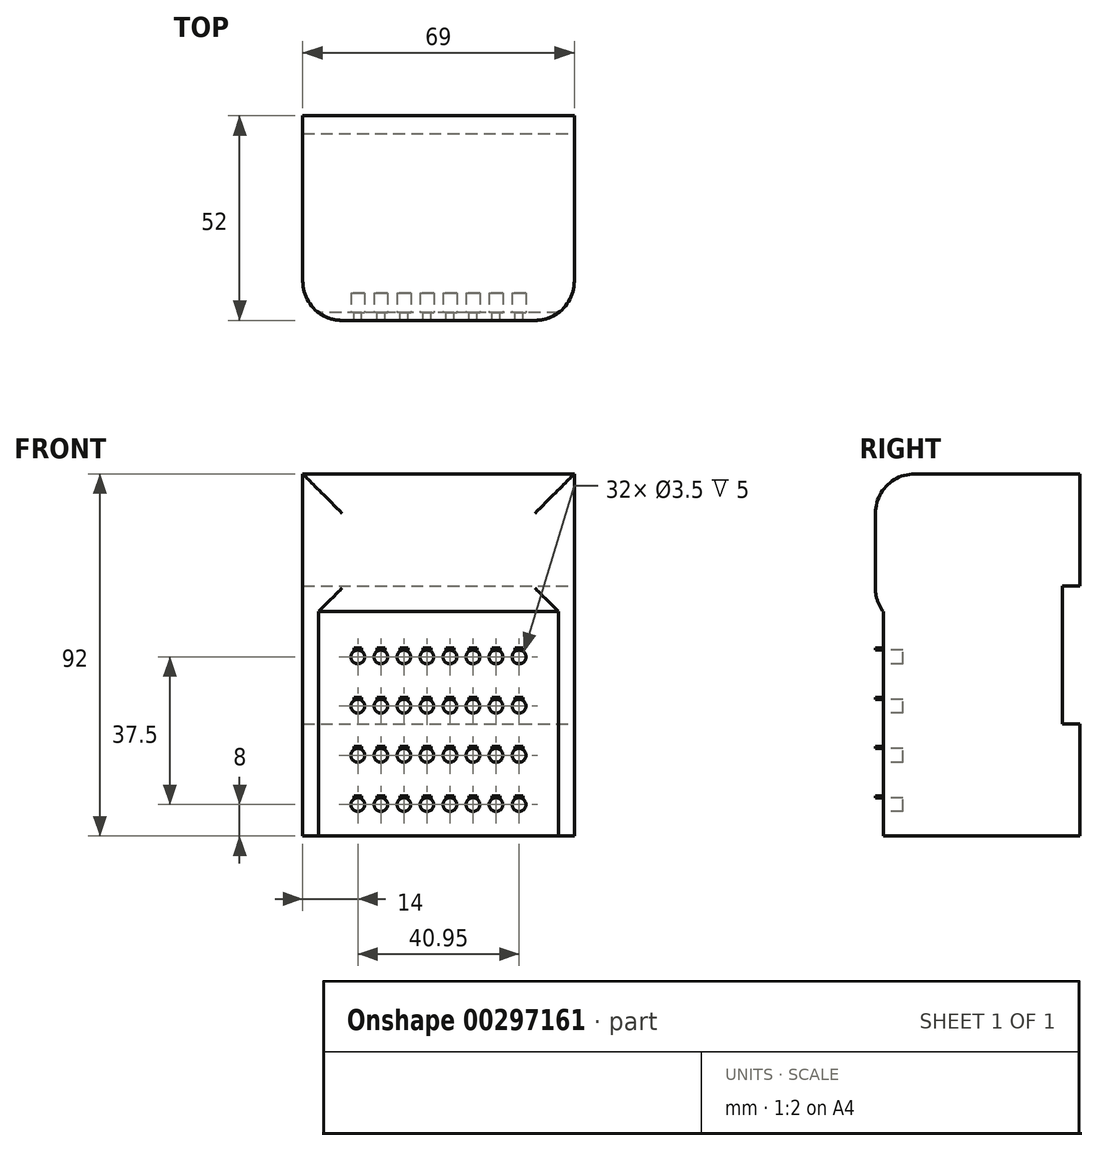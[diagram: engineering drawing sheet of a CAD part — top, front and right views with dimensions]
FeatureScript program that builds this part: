
annotation { "Feature Type Name" : "Feature", "Feature Type Description" : "" }
export const myFeature = defineFeature(function(context is Context, id is Id, definition is map)
    precondition{}
    {
        {
            var Q0;
            Q0=qCreatedBy(makeId("Front.planeOp"),FACE);
            var sketch = newSketch(context, id + "F0", { "sketchPlane" : qUnion([Q0])});
            skLineSegment(sketch, "E0.bottom", {"start": v(34.5, -46) * mm, "end": v(-34.5, -46) * mm});
            skLineSegment(sketch, "E0.top", {"start": v(34.5, 46) * mm, "end": v(-34.5, 46) * mm});
            skLineSegment(sketch, "E0.left", {"start": v(34.5, -46) * mm, "end": v(34.5, 46) * mm});
            skLineSegment(sketch, "E0.right", {"start": v(-34.5, -46) * mm, "end": v(-34.5, 46) * mm});
            skPoint(sketch, "E0.middle", {"position": v(0, 0) * mm});
            skSolve(sketch);
        }
        {
            var Q0;
            Q0=makeQuery(id+"F0.imprint","IMPRINT",FACE,{"disambiguationData":[TD([[makeQuery(id+"F0.imprint","IMPRINT",EDGE,{"derivedFrom":sQuery(id+"F0.wireOp",EDGE,"E0.bottom")}),-1.0]])]});
            extrude(context, id + "F1", {"entities" : qUnion([Q0]), "depth" : 50 * mm});
        }
        {
            var Q0;
            Q0=makeQuery(id+"F1.opExtrude","CAP_FACE",FACE,{"disambiguationData":[OSD([sQuery(id+"F0.wireOp",EDGE,"E0.bottom"),sQuery(id+"F0.wireOp",EDGE,"E0.top"),sQuery(id+"F0.wireOp",EDGE,"E0.left"),sQuery(id+"F0.wireOp",EDGE,"E0.right")])],"isStart":false});
            var sketch = newSketch(context, id + "F2", { "sketchPlane" : qUnion([Q0])});
            skLineSegment(sketch, "E1.bottom", {"start": v(-34.5, 46) * mm, "end": v(34.5, 46) * mm});
            skLineSegment(sketch, "E1.top", {"start": v(-34.5, 11) * mm, "end": v(34.5, 11) * mm});
            skLineSegment(sketch, "E1.left", {"start": v(-34.5, 46) * mm, "end": v(-34.5, 11) * mm});
            skLineSegment(sketch, "E1.right", {"start": v(34.5, 46) * mm, "end": v(34.5, 11) * mm});
            skSolve(sketch);
        }
        {
            var Q0;
            Q0=makeQuery(id+"F2.imprint","IMPRINT",FACE,{"disambiguationData":[TD([[makeQuery(id+"F2.imprint","IMPRINT",EDGE,{"derivedFrom":sQuery(id+"F2.wireOp",EDGE,"E1.bottom")}),1.0]])]});
            extrude(context, id + "F3", {"entities" : qUnion([Q0]), "operationType" : NewBodyOperationType.ADD, "depth" : 2 * mm});
        }
        {
            var Q0;
            Q0=makeQuery(id+"F3.opExtrude","CAP_FACE",FACE,{"disambiguationData":[OSD([sQuery(id+"F2.wireOp",EDGE,"E1.bottom"),sQuery(id+"F2.wireOp",EDGE,"E1.top"),sQuery(id+"F2.wireOp",EDGE,"E1.left"),sQuery(id+"F2.wireOp",EDGE,"E1.right")])],"isStart":false});
            fillet(context, id + "F4", {"entities" : qUnion([Q0]), "radius" : 10 * mm, "allowEdgeOverflow" : false});
        }
        {
            var Q0;
            Q0=makeQuery(id+"F1.opExtrude","CAP_FACE",FACE,{"disambiguationData":[OSD([sQuery(id+"F0.wireOp",EDGE,"E0.bottom"),sQuery(id+"F0.wireOp",EDGE,"E0.top"),sQuery(id+"F0.wireOp",EDGE,"E0.left"),sQuery(id+"F0.wireOp",EDGE,"E0.right")])],"isStart":false});
            var sketch = newSketch(context, id + "F5", { "sketchPlane" : qUnion([Q0])});
            skLineSegment(sketch, "E2", {"start": v(0, 11) * mm, "end": v(0, -46) * mm, "construction": true});
            skLineSegment(sketch, "E3", {"start": v(-30.5, -17.5) * mm, "end": v(30.5, -17.5) * mm, "construction": true});
            skLineSegment(sketch, "E4", {"start": v(-30.5, 11) * mm, "end": v(30.5, 11) * mm, "construction": true});
            skLineSegment(sketch, "E5", {"start": v(-30.5, -46) * mm, "end": v(30.5, -46) * mm, "construction": true});
            skLineSegment(sketch, "E6.0", {"start": v(-30.5, -0.5) * mm, "end": v(30.5, -0.5) * mm, "construction": true});
            skLineSegment(sketch, "E7.0", {"start": v(-30.5, -35) * mm, "end": v(30.5, -35) * mm, "construction": true});
            skLineSegment(sketch, "E8", {"start": v(-20.5, 11) * mm, "end": v(-20.5, -46) * mm, "construction": true});
            skLineSegment(sketch, "E9.MirrorCS", {"start": v(20.5, 11) * mm, "end": v(20.5, -46) * mm, "construction": true});
            skCircle(sketch, "E10", {"center": v(-20.5, -0.5) * mm, "radius": 1.75 * mm});
            skCircle(sketch, "E11.1.0.0", {"center": v(-14.65, -0.5) * mm, "radius": 1.75 * mm});
            skCircle(sketch, "E11.2.0.0", {"center": v(-8.8, -0.5) * mm, "radius": 1.75 * mm});
            skCircle(sketch, "E11.3.0.0", {"center": v(-2.95, -0.5) * mm, "radius": 1.75 * mm});
            skCircle(sketch, "E11.4.0.0", {"center": v(2.9, -0.5) * mm, "radius": 1.75 * mm});
            skCircle(sketch, "E11.5.0.0", {"center": v(8.75, -0.5) * mm, "radius": 1.75 * mm});
            skCircle(sketch, "E11.6.0.0", {"center": v(14.6, -0.5) * mm, "radius": 1.75 * mm});
            skCircle(sketch, "E11.7.0.0", {"center": v(20.45, -0.5) * mm, "radius": 1.75 * mm});
            skLineSegment(sketch, "E11.direction1", {"start": v(-20.5, -0.5) * mm, "end": v(-14.65, -0.5) * mm, "construction": true});
            skCircle(sketch, "E12.0.1.0", {"center": v(-20.5, -13) * mm, "radius": 1.75 * mm});
            skCircle(sketch, "E12.0.1.1", {"center": v(-14.65, -13) * mm, "radius": 1.75 * mm});
            skCircle(sketch, "E12.0.1.2", {"center": v(-8.8, -13) * mm, "radius": 1.75 * mm});
            skCircle(sketch, "E12.0.1.3", {"center": v(-2.95, -13) * mm, "radius": 1.75 * mm});
            skCircle(sketch, "E12.0.1.4", {"center": v(2.9, -13) * mm, "radius": 1.75 * mm});
            skCircle(sketch, "E12.0.1.5", {"center": v(8.75, -13) * mm, "radius": 1.75 * mm});
            skCircle(sketch, "E12.0.1.6", {"center": v(14.6, -13) * mm, "radius": 1.75 * mm});
            skCircle(sketch, "E12.0.1.7", {"center": v(20.45, -13) * mm, "radius": 1.75 * mm});
            skCircle(sketch, "E12.0.2.0", {"center": v(-20.5, -25.5) * mm, "radius": 1.75 * mm});
            skCircle(sketch, "E12.0.2.1", {"center": v(-14.65, -25.5) * mm, "radius": 1.75 * mm});
            skCircle(sketch, "E12.0.2.2", {"center": v(-8.8, -25.5) * mm, "radius": 1.75 * mm});
            skCircle(sketch, "E12.0.2.3", {"center": v(-2.95, -25.5) * mm, "radius": 1.75 * mm});
            skCircle(sketch, "E12.0.2.4", {"center": v(2.9, -25.5) * mm, "radius": 1.75 * mm});
            skCircle(sketch, "E12.0.2.5", {"center": v(8.75, -25.5) * mm, "radius": 1.75 * mm});
            skCircle(sketch, "E12.0.2.6", {"center": v(14.6, -25.5) * mm, "radius": 1.75 * mm});
            skCircle(sketch, "E12.0.2.7", {"center": v(20.45, -25.5) * mm, "radius": 1.75 * mm});
            skCircle(sketch, "E12.0.3.0", {"center": v(-20.5, -38) * mm, "radius": 1.75 * mm});
            skCircle(sketch, "E12.0.3.1", {"center": v(-14.65, -38) * mm, "radius": 1.75 * mm});
            skCircle(sketch, "E12.0.3.2", {"center": v(-8.8, -38) * mm, "radius": 1.75 * mm});
            skCircle(sketch, "E12.0.3.3", {"center": v(-2.95, -38) * mm, "radius": 1.75 * mm});
            skCircle(sketch, "E12.0.3.4", {"center": v(2.9, -38) * mm, "radius": 1.75 * mm});
            skCircle(sketch, "E12.0.3.5", {"center": v(8.75, -38) * mm, "radius": 1.75 * mm});
            skCircle(sketch, "E12.0.3.6", {"center": v(14.6, -38) * mm, "radius": 1.75 * mm});
            skCircle(sketch, "E12.0.3.7", {"center": v(20.45, -38) * mm, "radius": 1.75 * mm});
            skLineSegment(sketch, "E12.direction1", {"start": v(-20.5, -0.5) * mm, "end": v(47.4, -0.5) * mm, "construction": true});
            skLineSegment(sketch, "E12.direction2", {"start": v(-20.5, -0.5) * mm, "end": v(-20.5, -13) * mm, "construction": true});
            skLineSegment(sketch, "E13", {"start": v(-20.5, 1.25) * mm, "end": v(-19.5, 1.25) * mm});
            skLineSegment(sketch, "E14", {"start": v(-19.5, 1.25) * mm, "end": v(-19.5, 1.75) * mm});
            skLineSegment(sketch, "E15", {"start": v(-19.5, 1.75) * mm, "end": v(-21.5, 1.75) * mm});
            skLineSegment(sketch, "E16", {"start": v(-21.5, 1.75) * mm, "end": v(-21.5, 1.25) * mm});
            skLineSegment(sketch, "E17", {"start": v(-21.5, 1.25) * mm, "end": v(-20.5, 1.25) * mm});
            skLineSegment(sketch, "E18.0.1.0", {"start": v(-21.5, -10.75) * mm, "end": v(-21.5, -11.25) * mm});
            skLineSegment(sketch, "E18.0.1.1", {"start": v(-19.5, -10.75) * mm, "end": v(-21.5, -10.75) * mm});
            skLineSegment(sketch, "E18.0.1.2", {"start": v(-19.5, -11.25) * mm, "end": v(-19.5, -10.75) * mm});
            skLineSegment(sketch, "E18.0.1.3", {"start": v(-20.5, -11.25) * mm, "end": v(-19.5, -11.25) * mm});
            skLineSegment(sketch, "E18.0.1.4", {"start": v(-21.5, -11.25) * mm, "end": v(-20.5, -11.25) * mm});
            skLineSegment(sketch, "E18.0.2.0", {"start": v(-21.5, -23.25) * mm, "end": v(-21.5, -23.75) * mm});
            skLineSegment(sketch, "E18.0.2.1", {"start": v(-19.5, -23.25) * mm, "end": v(-21.5, -23.25) * mm});
            skLineSegment(sketch, "E18.0.2.2", {"start": v(-19.5, -23.75) * mm, "end": v(-19.5, -23.25) * mm});
            skLineSegment(sketch, "E18.0.2.3", {"start": v(-20.5, -23.75) * mm, "end": v(-19.5, -23.75) * mm});
            skLineSegment(sketch, "E18.0.2.4", {"start": v(-21.5, -23.75) * mm, "end": v(-20.5, -23.75) * mm});
            skLineSegment(sketch, "E18.0.3.0", {"start": v(-21.5, -35.75) * mm, "end": v(-21.5, -36.25) * mm});
            skLineSegment(sketch, "E18.0.3.1", {"start": v(-19.5, -35.75) * mm, "end": v(-21.5, -35.75) * mm});
            skLineSegment(sketch, "E18.0.3.2", {"start": v(-19.5, -36.25) * mm, "end": v(-19.5, -35.75) * mm});
            skLineSegment(sketch, "E18.0.3.3", {"start": v(-20.5, -36.25) * mm, "end": v(-19.5, -36.25) * mm});
            skLineSegment(sketch, "E18.0.3.4", {"start": v(-21.5, -36.25) * mm, "end": v(-20.5, -36.25) * mm});
            skLineSegment(sketch, "E18.1.0.0", {"start": v(-15.65, 1.75) * mm, "end": v(-15.65, 1.25) * mm});
            skLineSegment(sketch, "E18.1.0.1", {"start": v(-13.65, 1.75) * mm, "end": v(-15.65, 1.75) * mm});
            skLineSegment(sketch, "E18.1.0.2", {"start": v(-13.65, 1.25) * mm, "end": v(-13.65, 1.75) * mm});
            skLineSegment(sketch, "E18.1.0.3", {"start": v(-14.65, 1.25) * mm, "end": v(-13.65, 1.25) * mm});
            skLineSegment(sketch, "E18.1.0.4", {"start": v(-15.65, 1.25) * mm, "end": v(-14.65, 1.25) * mm});
            skLineSegment(sketch, "E18.1.1.0", {"start": v(-15.65, -10.75) * mm, "end": v(-15.65, -11.25) * mm});
            skLineSegment(sketch, "E18.1.1.1", {"start": v(-13.65, -10.75) * mm, "end": v(-15.65, -10.75) * mm});
            skLineSegment(sketch, "E18.1.1.2", {"start": v(-13.65, -11.25) * mm, "end": v(-13.65, -10.75) * mm});
            skLineSegment(sketch, "E18.1.1.3", {"start": v(-14.65, -11.25) * mm, "end": v(-13.65, -11.25) * mm});
            skLineSegment(sketch, "E18.1.1.4", {"start": v(-15.65, -11.25) * mm, "end": v(-14.65, -11.25) * mm});
            skLineSegment(sketch, "E18.1.2.0", {"start": v(-15.65, -23.25) * mm, "end": v(-15.65, -23.75) * mm});
            skLineSegment(sketch, "E18.1.2.1", {"start": v(-13.65, -23.25) * mm, "end": v(-15.65, -23.25) * mm});
            skLineSegment(sketch, "E18.1.2.2", {"start": v(-13.65, -23.75) * mm, "end": v(-13.65, -23.25) * mm});
            skLineSegment(sketch, "E18.1.2.3", {"start": v(-14.65, -23.75) * mm, "end": v(-13.65, -23.75) * mm});
            skLineSegment(sketch, "E18.1.2.4", {"start": v(-15.65, -23.75) * mm, "end": v(-14.65, -23.75) * mm});
            skLineSegment(sketch, "E18.1.3.0", {"start": v(-15.65, -35.75) * mm, "end": v(-15.65, -36.25) * mm});
            skLineSegment(sketch, "E18.1.3.1", {"start": v(-13.65, -35.75) * mm, "end": v(-15.65, -35.75) * mm});
            skLineSegment(sketch, "E18.1.3.2", {"start": v(-13.65, -36.25) * mm, "end": v(-13.65, -35.75) * mm});
            skLineSegment(sketch, "E18.1.3.3", {"start": v(-14.65, -36.25) * mm, "end": v(-13.65, -36.25) * mm});
            skLineSegment(sketch, "E18.1.3.4", {"start": v(-15.65, -36.25) * mm, "end": v(-14.65, -36.25) * mm});
            skLineSegment(sketch, "E18.2.0.0", {"start": v(-9.8, 1.75) * mm, "end": v(-9.8, 1.25) * mm});
            skLineSegment(sketch, "E18.2.0.1", {"start": v(-7.8, 1.75) * mm, "end": v(-9.8, 1.75) * mm});
            skLineSegment(sketch, "E18.2.0.2", {"start": v(-7.8, 1.25) * mm, "end": v(-7.8, 1.75) * mm});
            skLineSegment(sketch, "E18.2.0.3", {"start": v(-8.8, 1.25) * mm, "end": v(-7.8, 1.25) * mm});
            skLineSegment(sketch, "E18.2.0.4", {"start": v(-9.8, 1.25) * mm, "end": v(-8.8, 1.25) * mm});
            skLineSegment(sketch, "E18.2.1.0", {"start": v(-9.8, -10.75) * mm, "end": v(-9.8, -11.25) * mm});
            skLineSegment(sketch, "E18.2.1.1", {"start": v(-7.8, -10.75) * mm, "end": v(-9.8, -10.75) * mm});
            skLineSegment(sketch, "E18.2.1.2", {"start": v(-7.8, -11.25) * mm, "end": v(-7.8, -10.75) * mm});
            skLineSegment(sketch, "E18.2.1.3", {"start": v(-8.8, -11.25) * mm, "end": v(-7.8, -11.25) * mm});
            skLineSegment(sketch, "E18.2.1.4", {"start": v(-9.8, -11.25) * mm, "end": v(-8.8, -11.25) * mm});
            skLineSegment(sketch, "E18.2.2.0", {"start": v(-9.8, -23.25) * mm, "end": v(-9.8, -23.75) * mm});
            skLineSegment(sketch, "E18.2.2.1", {"start": v(-7.8, -23.25) * mm, "end": v(-9.8, -23.25) * mm});
            skLineSegment(sketch, "E18.2.2.2", {"start": v(-7.8, -23.75) * mm, "end": v(-7.8, -23.25) * mm});
            skLineSegment(sketch, "E18.2.2.3", {"start": v(-8.8, -23.75) * mm, "end": v(-7.8, -23.75) * mm});
            skLineSegment(sketch, "E18.2.2.4", {"start": v(-9.8, -23.75) * mm, "end": v(-8.8, -23.75) * mm});
            skLineSegment(sketch, "E18.2.3.0", {"start": v(-9.8, -35.75) * mm, "end": v(-9.8, -36.25) * mm});
            skLineSegment(sketch, "E18.2.3.1", {"start": v(-7.8, -35.75) * mm, "end": v(-9.8, -35.75) * mm});
            skLineSegment(sketch, "E18.2.3.2", {"start": v(-7.8, -36.25) * mm, "end": v(-7.8, -35.75) * mm});
            skLineSegment(sketch, "E18.2.3.3", {"start": v(-8.8, -36.25) * mm, "end": v(-7.8, -36.25) * mm});
            skLineSegment(sketch, "E18.2.3.4", {"start": v(-9.8, -36.25) * mm, "end": v(-8.8, -36.25) * mm});
            skLineSegment(sketch, "E18.3.0.0", {"start": v(-3.95, 1.75) * mm, "end": v(-3.95, 1.25) * mm});
            skLineSegment(sketch, "E18.3.0.1", {"start": v(-1.95, 1.75) * mm, "end": v(-3.95, 1.75) * mm});
            skLineSegment(sketch, "E18.3.0.2", {"start": v(-1.95, 1.25) * mm, "end": v(-1.95, 1.75) * mm});
            skLineSegment(sketch, "E18.3.0.3", {"start": v(-2.95, 1.25) * mm, "end": v(-1.95, 1.25) * mm});
            skLineSegment(sketch, "E18.3.0.4", {"start": v(-3.95, 1.25) * mm, "end": v(-2.95, 1.25) * mm});
            skLineSegment(sketch, "E18.3.1.0", {"start": v(-3.95, -10.75) * mm, "end": v(-3.95, -11.25) * mm});
            skLineSegment(sketch, "E18.3.1.1", {"start": v(-1.95, -10.75) * mm, "end": v(-3.95, -10.75) * mm});
            skLineSegment(sketch, "E18.3.1.2", {"start": v(-1.95, -11.25) * mm, "end": v(-1.95, -10.75) * mm});
            skLineSegment(sketch, "E18.3.1.3", {"start": v(-2.95, -11.25) * mm, "end": v(-1.95, -11.25) * mm});
            skLineSegment(sketch, "E18.3.1.4", {"start": v(-3.95, -11.25) * mm, "end": v(-2.95, -11.25) * mm});
            skLineSegment(sketch, "E18.3.2.0", {"start": v(-3.95, -23.25) * mm, "end": v(-3.95, -23.75) * mm});
            skLineSegment(sketch, "E18.3.2.1", {"start": v(-1.95, -23.25) * mm, "end": v(-3.95, -23.25) * mm});
            skLineSegment(sketch, "E18.3.2.2", {"start": v(-1.95, -23.75) * mm, "end": v(-1.95, -23.25) * mm});
            skLineSegment(sketch, "E18.3.2.3", {"start": v(-2.95, -23.75) * mm, "end": v(-1.95, -23.75) * mm});
            skLineSegment(sketch, "E18.3.2.4", {"start": v(-3.95, -23.75) * mm, "end": v(-2.95, -23.75) * mm});
            skLineSegment(sketch, "E18.3.3.0", {"start": v(-3.95, -35.75) * mm, "end": v(-3.95, -36.25) * mm});
            skLineSegment(sketch, "E18.3.3.1", {"start": v(-1.95, -35.75) * mm, "end": v(-3.95, -35.75) * mm});
            skLineSegment(sketch, "E18.3.3.2", {"start": v(-1.95, -36.25) * mm, "end": v(-1.95, -35.75) * mm});
            skLineSegment(sketch, "E18.3.3.3", {"start": v(-2.95, -36.25) * mm, "end": v(-1.95, -36.25) * mm});
            skLineSegment(sketch, "E18.3.3.4", {"start": v(-3.95, -36.25) * mm, "end": v(-2.95, -36.25) * mm});
            skLineSegment(sketch, "E18.4.0.0", {"start": v(1.9, 1.75) * mm, "end": v(1.9, 1.25) * mm});
            skLineSegment(sketch, "E18.4.0.1", {"start": v(3.9, 1.75) * mm, "end": v(1.9, 1.75) * mm});
            skLineSegment(sketch, "E18.4.0.2", {"start": v(3.9, 1.25) * mm, "end": v(3.9, 1.75) * mm});
            skLineSegment(sketch, "E18.4.0.3", {"start": v(2.9, 1.25) * mm, "end": v(3.9, 1.25) * mm});
            skLineSegment(sketch, "E18.4.0.4", {"start": v(1.9, 1.25) * mm, "end": v(2.9, 1.25) * mm});
            skLineSegment(sketch, "E18.4.1.0", {"start": v(1.9, -10.75) * mm, "end": v(1.9, -11.25) * mm});
            skLineSegment(sketch, "E18.4.1.1", {"start": v(3.9, -10.75) * mm, "end": v(1.9, -10.75) * mm});
            skLineSegment(sketch, "E18.4.1.2", {"start": v(3.9, -11.25) * mm, "end": v(3.9, -10.75) * mm});
            skLineSegment(sketch, "E18.4.1.3", {"start": v(2.9, -11.25) * mm, "end": v(3.9, -11.25) * mm});
            skLineSegment(sketch, "E18.4.1.4", {"start": v(1.9, -11.25) * mm, "end": v(2.9, -11.25) * mm});
            skLineSegment(sketch, "E18.4.2.0", {"start": v(1.9, -23.25) * mm, "end": v(1.9, -23.75) * mm});
            skLineSegment(sketch, "E18.4.2.1", {"start": v(3.9, -23.25) * mm, "end": v(1.9, -23.25) * mm});
            skLineSegment(sketch, "E18.4.2.2", {"start": v(3.9, -23.75) * mm, "end": v(3.9, -23.25) * mm});
            skLineSegment(sketch, "E18.4.2.3", {"start": v(2.9, -23.75) * mm, "end": v(3.9, -23.75) * mm});
            skLineSegment(sketch, "E18.4.2.4", {"start": v(1.9, -23.75) * mm, "end": v(2.9, -23.75) * mm});
            skLineSegment(sketch, "E18.4.3.0", {"start": v(1.9, -35.75) * mm, "end": v(1.9, -36.25) * mm});
            skLineSegment(sketch, "E18.4.3.1", {"start": v(3.9, -35.75) * mm, "end": v(1.9, -35.75) * mm});
            skLineSegment(sketch, "E18.4.3.2", {"start": v(3.9, -36.25) * mm, "end": v(3.9, -35.75) * mm});
            skLineSegment(sketch, "E18.4.3.3", {"start": v(2.9, -36.25) * mm, "end": v(3.9, -36.25) * mm});
            skLineSegment(sketch, "E18.4.3.4", {"start": v(1.9, -36.25) * mm, "end": v(2.9, -36.25) * mm});
            skLineSegment(sketch, "E18.5.0.0", {"start": v(7.75, 1.75) * mm, "end": v(7.75, 1.25) * mm});
            skLineSegment(sketch, "E18.5.0.1", {"start": v(9.75, 1.75) * mm, "end": v(7.75, 1.75) * mm});
            skLineSegment(sketch, "E18.5.0.2", {"start": v(9.75, 1.25) * mm, "end": v(9.75, 1.75) * mm});
            skLineSegment(sketch, "E18.5.0.3", {"start": v(8.75, 1.25) * mm, "end": v(9.75, 1.25) * mm});
            skLineSegment(sketch, "E18.5.0.4", {"start": v(7.75, 1.25) * mm, "end": v(8.75, 1.25) * mm});
            skLineSegment(sketch, "E18.5.1.0", {"start": v(7.75, -10.75) * mm, "end": v(7.75, -11.25) * mm});
            skLineSegment(sketch, "E18.5.1.1", {"start": v(9.75, -10.75) * mm, "end": v(7.75, -10.75) * mm});
            skLineSegment(sketch, "E18.5.1.2", {"start": v(9.75, -11.25) * mm, "end": v(9.75, -10.75) * mm});
            skLineSegment(sketch, "E18.5.1.3", {"start": v(8.75, -11.25) * mm, "end": v(9.75, -11.25) * mm});
            skLineSegment(sketch, "E18.5.1.4", {"start": v(7.75, -11.25) * mm, "end": v(8.75, -11.25) * mm});
            skLineSegment(sketch, "E18.5.2.0", {"start": v(7.75, -23.25) * mm, "end": v(7.75, -23.75) * mm});
            skLineSegment(sketch, "E18.5.2.1", {"start": v(9.75, -23.25) * mm, "end": v(7.75, -23.25) * mm});
            skLineSegment(sketch, "E18.5.2.2", {"start": v(9.75, -23.75) * mm, "end": v(9.75, -23.25) * mm});
            skLineSegment(sketch, "E18.5.2.3", {"start": v(8.75, -23.75) * mm, "end": v(9.75, -23.75) * mm});
            skLineSegment(sketch, "E18.5.2.4", {"start": v(7.75, -23.75) * mm, "end": v(8.75, -23.75) * mm});
            skLineSegment(sketch, "E18.5.3.0", {"start": v(7.75, -35.75) * mm, "end": v(7.75, -36.25) * mm});
            skLineSegment(sketch, "E18.5.3.1", {"start": v(9.75, -35.75) * mm, "end": v(7.75, -35.75) * mm});
            skLineSegment(sketch, "E18.5.3.2", {"start": v(9.75, -36.25) * mm, "end": v(9.75, -35.75) * mm});
            skLineSegment(sketch, "E18.5.3.3", {"start": v(8.75, -36.25) * mm, "end": v(9.75, -36.25) * mm});
            skLineSegment(sketch, "E18.5.3.4", {"start": v(7.75, -36.25) * mm, "end": v(8.75, -36.25) * mm});
            skLineSegment(sketch, "E18.6.0.0", {"start": v(13.6, 1.75) * mm, "end": v(13.6, 1.25) * mm});
            skLineSegment(sketch, "E18.6.0.1", {"start": v(15.6, 1.75) * mm, "end": v(13.6, 1.75) * mm});
            skLineSegment(sketch, "E18.6.0.2", {"start": v(15.6, 1.25) * mm, "end": v(15.6, 1.75) * mm});
            skLineSegment(sketch, "E18.6.0.3", {"start": v(14.6, 1.25) * mm, "end": v(15.6, 1.25) * mm});
            skLineSegment(sketch, "E18.6.0.4", {"start": v(13.6, 1.25) * mm, "end": v(14.6, 1.25) * mm});
            skLineSegment(sketch, "E18.6.1.0", {"start": v(13.6, -10.75) * mm, "end": v(13.6, -11.25) * mm});
            skLineSegment(sketch, "E18.6.1.1", {"start": v(15.6, -10.75) * mm, "end": v(13.6, -10.75) * mm});
            skLineSegment(sketch, "E18.6.1.2", {"start": v(15.6, -11.25) * mm, "end": v(15.6, -10.75) * mm});
            skLineSegment(sketch, "E18.6.1.3", {"start": v(14.6, -11.25) * mm, "end": v(15.6, -11.25) * mm});
            skLineSegment(sketch, "E18.6.1.4", {"start": v(13.6, -11.25) * mm, "end": v(14.6, -11.25) * mm});
            skLineSegment(sketch, "E18.6.2.0", {"start": v(13.6, -23.25) * mm, "end": v(13.6, -23.75) * mm});
            skLineSegment(sketch, "E18.6.2.1", {"start": v(15.6, -23.25) * mm, "end": v(13.6, -23.25) * mm});
            skLineSegment(sketch, "E18.6.2.2", {"start": v(15.6, -23.75) * mm, "end": v(15.6, -23.25) * mm});
            skLineSegment(sketch, "E18.6.2.3", {"start": v(14.6, -23.75) * mm, "end": v(15.6, -23.75) * mm});
            skLineSegment(sketch, "E18.6.2.4", {"start": v(13.6, -23.75) * mm, "end": v(14.6, -23.75) * mm});
            skLineSegment(sketch, "E18.6.3.0", {"start": v(13.6, -35.75) * mm, "end": v(13.6, -36.25) * mm});
            skLineSegment(sketch, "E18.6.3.1", {"start": v(15.6, -35.75) * mm, "end": v(13.6, -35.75) * mm});
            skLineSegment(sketch, "E18.6.3.2", {"start": v(15.6, -36.25) * mm, "end": v(15.6, -35.75) * mm});
            skLineSegment(sketch, "E18.6.3.3", {"start": v(14.6, -36.25) * mm, "end": v(15.6, -36.25) * mm});
            skLineSegment(sketch, "E18.6.3.4", {"start": v(13.6, -36.25) * mm, "end": v(14.6, -36.25) * mm});
            skLineSegment(sketch, "E18.7.0.0", {"start": v(19.45, 1.75) * mm, "end": v(19.45, 1.25) * mm});
            skLineSegment(sketch, "E18.7.0.1", {"start": v(21.45, 1.75) * mm, "end": v(19.45, 1.75) * mm});
            skLineSegment(sketch, "E18.7.0.2", {"start": v(21.45, 1.25) * mm, "end": v(21.45, 1.75) * mm});
            skLineSegment(sketch, "E18.7.0.3", {"start": v(20.45, 1.25) * mm, "end": v(21.45, 1.25) * mm});
            skLineSegment(sketch, "E18.7.0.4", {"start": v(19.45, 1.25) * mm, "end": v(20.45, 1.25) * mm});
            skLineSegment(sketch, "E18.7.1.0", {"start": v(19.45, -10.75) * mm, "end": v(19.45, -11.25) * mm});
            skLineSegment(sketch, "E18.7.1.1", {"start": v(21.45, -10.75) * mm, "end": v(19.45, -10.75) * mm});
            skLineSegment(sketch, "E18.7.1.2", {"start": v(21.45, -11.25) * mm, "end": v(21.45, -10.75) * mm});
            skLineSegment(sketch, "E18.7.1.3", {"start": v(20.45, -11.25) * mm, "end": v(21.45, -11.25) * mm});
            skLineSegment(sketch, "E18.7.1.4", {"start": v(19.45, -11.25) * mm, "end": v(20.45, -11.25) * mm});
            skLineSegment(sketch, "E18.7.2.0", {"start": v(19.45, -23.25) * mm, "end": v(19.45, -23.75) * mm});
            skLineSegment(sketch, "E18.7.2.1", {"start": v(21.45, -23.25) * mm, "end": v(19.45, -23.25) * mm});
            skLineSegment(sketch, "E18.7.2.2", {"start": v(21.45, -23.75) * mm, "end": v(21.45, -23.25) * mm});
            skLineSegment(sketch, "E18.7.2.3", {"start": v(20.45, -23.75) * mm, "end": v(21.45, -23.75) * mm});
            skLineSegment(sketch, "E18.7.2.4", {"start": v(19.45, -23.75) * mm, "end": v(20.45, -23.75) * mm});
            skLineSegment(sketch, "E18.7.3.0", {"start": v(19.45, -35.75) * mm, "end": v(19.45, -36.25) * mm});
            skLineSegment(sketch, "E18.7.3.1", {"start": v(21.45, -35.75) * mm, "end": v(19.45, -35.75) * mm});
            skLineSegment(sketch, "E18.7.3.2", {"start": v(21.45, -36.25) * mm, "end": v(21.45, -35.75) * mm});
            skLineSegment(sketch, "E18.7.3.3", {"start": v(20.45, -36.25) * mm, "end": v(21.45, -36.25) * mm});
            skLineSegment(sketch, "E18.7.3.4", {"start": v(19.45, -36.25) * mm, "end": v(20.45, -36.25) * mm});
            skLineSegment(sketch, "E18.direction1", {"start": v(-21.5, 1.25) * mm, "end": v(-15.65, 1.25) * mm, "construction": true});
            skLineSegment(sketch, "E18.direction2", {"start": v(-21.5, 1.25) * mm, "end": v(-21.5, -11.25) * mm, "construction": true});
            skSolve(sketch);
        }
        {
            var Q0;
            Q0=makeQuery(id+"F5.imprint","IMPRINT",FACE,{"disambiguationData":[TD([[makeQuery(id+"F5.imprint","IMPRINT",EDGE,{"derivedFrom":sQuery(id+"F5.wireOp",EDGE,"E10")}),1.0]])]});
            var Q1;
            Q1=makeQuery(id+"F5.imprint","IMPRINT",FACE,{"disambiguationData":[TD([[makeQuery(id+"F5.imprint","IMPRINT",EDGE,{"derivedFrom":sQuery(id+"F5.wireOp",EDGE,"E11.1.0.0")}),1.0]])]});
            var Q2;
            Q2=makeQuery(id+"F5.imprint","IMPRINT",FACE,{"disambiguationData":[TD([[makeQuery(id+"F5.imprint","IMPRINT",EDGE,{"derivedFrom":sQuery(id+"F5.wireOp",EDGE,"E11.2.0.0")}),1.0]])]});
            var Q3;
            Q3=makeQuery(id+"F5.imprint","IMPRINT",FACE,{"disambiguationData":[TD([[makeQuery(id+"F5.imprint","IMPRINT",EDGE,{"derivedFrom":sQuery(id+"F5.wireOp",EDGE,"E11.3.0.0")}),1.0]])]});
            var Q4;
            Q4=makeQuery(id+"F5.imprint","IMPRINT",FACE,{"disambiguationData":[TD([[makeQuery(id+"F5.imprint","IMPRINT",EDGE,{"derivedFrom":sQuery(id+"F5.wireOp",EDGE,"E11.4.0.0")}),1.0]])]});
            var Q5;
            Q5=makeQuery(id+"F5.imprint","IMPRINT",FACE,{"disambiguationData":[TD([[makeQuery(id+"F5.imprint","IMPRINT",EDGE,{"derivedFrom":sQuery(id+"F5.wireOp",EDGE,"E11.5.0.0")}),1.0]])]});
            var Q6;
            Q6=makeQuery(id+"F5.imprint","IMPRINT",FACE,{"disambiguationData":[TD([[makeQuery(id+"F5.imprint","IMPRINT",EDGE,{"derivedFrom":sQuery(id+"F5.wireOp",EDGE,"E11.6.0.0")}),1.0]])]});
            var Q7;
            Q7=makeQuery(id+"F5.imprint","IMPRINT",FACE,{"disambiguationData":[TD([[makeQuery(id+"F5.imprint","IMPRINT",EDGE,{"derivedFrom":sQuery(id+"F5.wireOp",EDGE,"E11.7.0.0")}),1.0]])]});
            var Q8;
            Q8=makeQuery(id+"F5.imprint","IMPRINT",FACE,{"disambiguationData":[TD([[makeQuery(id+"F5.imprint","IMPRINT",EDGE,{"derivedFrom":sQuery(id+"F5.wireOp",EDGE,"E12.0.1.0")}),1.0]])]});
            var Q9;
            Q9=makeQuery(id+"F5.imprint","IMPRINT",FACE,{"disambiguationData":[TD([[makeQuery(id+"F5.imprint","IMPRINT",EDGE,{"derivedFrom":sQuery(id+"F5.wireOp",EDGE,"E12.0.1.1")}),1.0]])]});
            var Q10;
            Q10=makeQuery(id+"F5.imprint","IMPRINT",FACE,{"disambiguationData":[TD([[makeQuery(id+"F5.imprint","IMPRINT",EDGE,{"derivedFrom":sQuery(id+"F5.wireOp",EDGE,"E12.0.1.2")}),1.0]])]});
            var Q11;
            Q11=makeQuery(id+"F5.imprint","IMPRINT",FACE,{"disambiguationData":[TD([[makeQuery(id+"F5.imprint","IMPRINT",EDGE,{"derivedFrom":sQuery(id+"F5.wireOp",EDGE,"E12.0.1.3")}),1.0]])]});
            var Q12;
            Q12=makeQuery(id+"F5.imprint","IMPRINT",FACE,{"disambiguationData":[TD([[makeQuery(id+"F5.imprint","IMPRINT",EDGE,{"derivedFrom":sQuery(id+"F5.wireOp",EDGE,"E12.0.1.4")}),1.0]])]});
            var Q13;
            Q13=makeQuery(id+"F5.imprint","IMPRINT",FACE,{"disambiguationData":[TD([[makeQuery(id+"F5.imprint","IMPRINT",EDGE,{"derivedFrom":sQuery(id+"F5.wireOp",EDGE,"E12.0.1.5")}),1.0]])]});
            var Q14;
            Q14=makeQuery(id+"F5.imprint","IMPRINT",FACE,{"disambiguationData":[TD([[makeQuery(id+"F5.imprint","IMPRINT",EDGE,{"derivedFrom":sQuery(id+"F5.wireOp",EDGE,"E12.0.1.6")}),1.0]])]});
            var Q15;
            Q15=makeQuery(id+"F5.imprint","IMPRINT",FACE,{"disambiguationData":[TD([[makeQuery(id+"F5.imprint","IMPRINT",EDGE,{"derivedFrom":sQuery(id+"F5.wireOp",EDGE,"E12.0.1.7")}),1.0]])]});
            var Q16;
            Q16=makeQuery(id+"F5.imprint","IMPRINT",FACE,{"disambiguationData":[TD([[makeQuery(id+"F5.imprint","IMPRINT",EDGE,{"derivedFrom":sQuery(id+"F5.wireOp",EDGE,"E12.0.2.7")}),1.0]])]});
            var Q17;
            Q17=makeQuery(id+"F5.imprint","IMPRINT",FACE,{"disambiguationData":[TD([[makeQuery(id+"F5.imprint","IMPRINT",EDGE,{"derivedFrom":sQuery(id+"F5.wireOp",EDGE,"E12.0.2.6")}),1.0]])]});
            var Q18;
            Q18=makeQuery(id+"F5.imprint","IMPRINT",FACE,{"disambiguationData":[TD([[makeQuery(id+"F5.imprint","IMPRINT",EDGE,{"derivedFrom":sQuery(id+"F5.wireOp",EDGE,"E12.0.2.5")}),1.0]])]});
            var Q19;
            Q19=makeQuery(id+"F5.imprint","IMPRINT",FACE,{"disambiguationData":[TD([[makeQuery(id+"F5.imprint","IMPRINT",EDGE,{"derivedFrom":sQuery(id+"F5.wireOp",EDGE,"E12.0.2.4")}),1.0]])]});
            var Q20;
            Q20=makeQuery(id+"F5.imprint","IMPRINT",FACE,{"disambiguationData":[TD([[makeQuery(id+"F5.imprint","IMPRINT",EDGE,{"derivedFrom":sQuery(id+"F5.wireOp",EDGE,"E12.0.2.3")}),1.0]])]});
            var Q21;
            Q21=makeQuery(id+"F5.imprint","IMPRINT",FACE,{"disambiguationData":[TD([[makeQuery(id+"F5.imprint","IMPRINT",EDGE,{"derivedFrom":sQuery(id+"F5.wireOp",EDGE,"E12.0.2.2")}),1.0]])]});
            var Q22;
            Q22=makeQuery(id+"F5.imprint","IMPRINT",FACE,{"disambiguationData":[TD([[makeQuery(id+"F5.imprint","IMPRINT",EDGE,{"derivedFrom":sQuery(id+"F5.wireOp",EDGE,"E12.0.2.1")}),1.0]])]});
            var Q23;
            Q23=makeQuery(id+"F5.imprint","IMPRINT",FACE,{"disambiguationData":[TD([[makeQuery(id+"F5.imprint","IMPRINT",EDGE,{"derivedFrom":sQuery(id+"F5.wireOp",EDGE,"E12.0.2.0")}),1.0]])]});
            var Q24;
            Q24=makeQuery(id+"F5.imprint","IMPRINT",FACE,{"disambiguationData":[TD([[makeQuery(id+"F5.imprint","IMPRINT",EDGE,{"derivedFrom":sQuery(id+"F5.wireOp",EDGE,"E12.0.3.0")}),1.0]])]});
            var Q25;
            Q25=makeQuery(id+"F5.imprint","IMPRINT",FACE,{"disambiguationData":[TD([[makeQuery(id+"F5.imprint","IMPRINT",EDGE,{"derivedFrom":sQuery(id+"F5.wireOp",EDGE,"E12.0.3.1")}),1.0]])]});
            var Q26;
            Q26=makeQuery(id+"F5.imprint","IMPRINT",FACE,{"disambiguationData":[TD([[makeQuery(id+"F5.imprint","IMPRINT",EDGE,{"derivedFrom":sQuery(id+"F5.wireOp",EDGE,"E12.0.3.2")}),1.0]])]});
            var Q27;
            Q27=makeQuery(id+"F5.imprint","IMPRINT",FACE,{"disambiguationData":[TD([[makeQuery(id+"F5.imprint","IMPRINT",EDGE,{"derivedFrom":sQuery(id+"F5.wireOp",EDGE,"E12.0.3.3")}),1.0]])]});
            var Q28;
            Q28=makeQuery(id+"F5.imprint","IMPRINT",FACE,{"disambiguationData":[TD([[makeQuery(id+"F5.imprint","IMPRINT",EDGE,{"derivedFrom":sQuery(id+"F5.wireOp",EDGE,"E12.0.3.4")}),1.0]])]});
            var Q29;
            Q29=makeQuery(id+"F5.imprint","IMPRINT",FACE,{"disambiguationData":[TD([[makeQuery(id+"F5.imprint","IMPRINT",EDGE,{"derivedFrom":sQuery(id+"F5.wireOp",EDGE,"E12.0.3.5")}),1.0]])]});
            var Q30;
            Q30=makeQuery(id+"F5.imprint","IMPRINT",FACE,{"disambiguationData":[TD([[makeQuery(id+"F5.imprint","IMPRINT",EDGE,{"derivedFrom":sQuery(id+"F5.wireOp",EDGE,"E12.0.3.6")}),1.0]])]});
            var Q31;
            Q31=makeQuery(id+"F5.imprint","IMPRINT",FACE,{"disambiguationData":[TD([[makeQuery(id+"F5.imprint","IMPRINT",EDGE,{"derivedFrom":sQuery(id+"F5.wireOp",EDGE,"E12.0.3.7")}),1.0]])]});
            extrude(context, id + "F6", {"entities" : qUnion([Q0, Q1, Q2, Q3, Q4, Q5, Q6, Q7, Q8, Q9, Q10, Q11, Q12, Q13, Q14, Q15, Q16, Q17, Q18, Q19, Q20, Q21, Q22, Q23, Q24, Q25, Q26, Q27, Q28, Q29, Q30, Q31]), "operationType" : NewBodyOperationType.REMOVE, "oppositeDirection" : true, "depth" : 5 * mm});
        }
        {
            var Q0;
            Q0=makeQuery(id+"F5.imprint","IMPRINT",FACE,{"disambiguationData":[TD([[makeQuery(id+"F5.imprint","IMPRINT",EDGE,{"derivedFrom":sQuery(id+"F5.wireOp",EDGE,"E13")}),1.0]])]});
            var Q1;
            Q1=makeQuery(id+"F5.imprint","IMPRINT",FACE,{"disambiguationData":[TD([[makeQuery(id+"F5.imprint","IMPRINT",EDGE,{"derivedFrom":sQuery(id+"F5.wireOp",EDGE,"E18.1.0.0")}),1.0]])]});
            var Q2;
            Q2=makeQuery(id+"F5.imprint","IMPRINT",FACE,{"disambiguationData":[TD([[makeQuery(id+"F5.imprint","IMPRINT",EDGE,{"derivedFrom":sQuery(id+"F5.wireOp",EDGE,"E18.2.0.0")}),1.0]])]});
            var Q3;
            Q3=makeQuery(id+"F5.imprint","IMPRINT",FACE,{"disambiguationData":[TD([[makeQuery(id+"F5.imprint","IMPRINT",EDGE,{"derivedFrom":sQuery(id+"F5.wireOp",EDGE,"E18.3.0.0")}),1.0]])]});
            var Q4;
            Q4=makeQuery(id+"F5.imprint","IMPRINT",FACE,{"disambiguationData":[TD([[makeQuery(id+"F5.imprint","IMPRINT",EDGE,{"derivedFrom":sQuery(id+"F5.wireOp",EDGE,"E18.4.0.0")}),1.0]])]});
            var Q5;
            Q5=makeQuery(id+"F5.imprint","IMPRINT",FACE,{"disambiguationData":[TD([[makeQuery(id+"F5.imprint","IMPRINT",EDGE,{"derivedFrom":sQuery(id+"F5.wireOp",EDGE,"E18.5.0.0")}),1.0]])]});
            var Q6;
            Q6=makeQuery(id+"F5.imprint","IMPRINT",FACE,{"disambiguationData":[TD([[makeQuery(id+"F5.imprint","IMPRINT",EDGE,{"derivedFrom":sQuery(id+"F5.wireOp",EDGE,"E18.6.0.0")}),1.0]])]});
            var Q7;
            Q7=makeQuery(id+"F5.imprint","IMPRINT",FACE,{"disambiguationData":[TD([[makeQuery(id+"F5.imprint","IMPRINT",EDGE,{"derivedFrom":sQuery(id+"F5.wireOp",EDGE,"E18.7.0.0")}),1.0]])]});
            var Q8;
            Q8=makeQuery(id+"F5.imprint","IMPRINT",FACE,{"disambiguationData":[TD([[makeQuery(id+"F5.imprint","IMPRINT",EDGE,{"derivedFrom":sQuery(id+"F5.wireOp",EDGE,"E18.0.1.0")}),1.0]])]});
            var Q9;
            Q9=makeQuery(id+"F5.imprint","IMPRINT",FACE,{"disambiguationData":[TD([[makeQuery(id+"F5.imprint","IMPRINT",EDGE,{"derivedFrom":sQuery(id+"F5.wireOp",EDGE,"E18.1.1.0")}),1.0]])]});
            var Q10;
            Q10=makeQuery(id+"F5.imprint","IMPRINT",FACE,{"disambiguationData":[TD([[makeQuery(id+"F5.imprint","IMPRINT",EDGE,{"derivedFrom":sQuery(id+"F5.wireOp",EDGE,"E18.2.1.0")}),1.0]])]});
            var Q11;
            Q11=makeQuery(id+"F5.imprint","IMPRINT",FACE,{"disambiguationData":[TD([[makeQuery(id+"F5.imprint","IMPRINT",EDGE,{"derivedFrom":sQuery(id+"F5.wireOp",EDGE,"E18.3.1.0")}),1.0]])]});
            var Q12;
            Q12=makeQuery(id+"F5.imprint","IMPRINT",FACE,{"disambiguationData":[TD([[makeQuery(id+"F5.imprint","IMPRINT",EDGE,{"derivedFrom":sQuery(id+"F5.wireOp",EDGE,"E18.4.1.0")}),1.0]])]});
            var Q13;
            Q13=makeQuery(id+"F5.imprint","IMPRINT",FACE,{"disambiguationData":[TD([[makeQuery(id+"F5.imprint","IMPRINT",EDGE,{"derivedFrom":sQuery(id+"F5.wireOp",EDGE,"E18.5.1.0")}),1.0]])]});
            var Q14;
            Q14=makeQuery(id+"F5.imprint","IMPRINT",FACE,{"disambiguationData":[TD([[makeQuery(id+"F5.imprint","IMPRINT",EDGE,{"derivedFrom":sQuery(id+"F5.wireOp",EDGE,"E18.6.1.0")}),1.0]])]});
            var Q15;
            Q15=makeQuery(id+"F5.imprint","IMPRINT",FACE,{"disambiguationData":[TD([[makeQuery(id+"F5.imprint","IMPRINT",EDGE,{"derivedFrom":sQuery(id+"F5.wireOp",EDGE,"E18.7.1.0")}),1.0]])]});
            var Q16;
            Q16=makeQuery(id+"F5.imprint","IMPRINT",FACE,{"disambiguationData":[TD([[makeQuery(id+"F5.imprint","IMPRINT",EDGE,{"derivedFrom":sQuery(id+"F5.wireOp",EDGE,"E18.0.2.0")}),1.0]])]});
            var Q17;
            Q17=makeQuery(id+"F5.imprint","IMPRINT",FACE,{"disambiguationData":[TD([[makeQuery(id+"F5.imprint","IMPRINT",EDGE,{"derivedFrom":sQuery(id+"F5.wireOp",EDGE,"E18.1.2.0")}),1.0]])]});
            var Q18;
            Q18=makeQuery(id+"F5.imprint","IMPRINT",FACE,{"disambiguationData":[TD([[makeQuery(id+"F5.imprint","IMPRINT",EDGE,{"derivedFrom":sQuery(id+"F5.wireOp",EDGE,"E18.2.2.0")}),1.0]])]});
            var Q19;
            Q19=makeQuery(id+"F5.imprint","IMPRINT",FACE,{"disambiguationData":[TD([[makeQuery(id+"F5.imprint","IMPRINT",EDGE,{"derivedFrom":sQuery(id+"F5.wireOp",EDGE,"E18.3.2.0")}),1.0]])]});
            var Q20;
            Q20=makeQuery(id+"F5.imprint","IMPRINT",FACE,{"disambiguationData":[TD([[makeQuery(id+"F5.imprint","IMPRINT",EDGE,{"derivedFrom":sQuery(id+"F5.wireOp",EDGE,"E18.4.2.0")}),1.0]])]});
            var Q21;
            Q21=makeQuery(id+"F5.imprint","IMPRINT",FACE,{"disambiguationData":[TD([[makeQuery(id+"F5.imprint","IMPRINT",EDGE,{"derivedFrom":sQuery(id+"F5.wireOp",EDGE,"E18.5.2.0")}),1.0]])]});
            var Q22;
            Q22=makeQuery(id+"F5.imprint","IMPRINT",FACE,{"disambiguationData":[TD([[makeQuery(id+"F5.imprint","IMPRINT",EDGE,{"derivedFrom":sQuery(id+"F5.wireOp",EDGE,"E18.6.2.0")}),1.0]])]});
            var Q23;
            Q23=makeQuery(id+"F5.imprint","IMPRINT",FACE,{"disambiguationData":[TD([[makeQuery(id+"F5.imprint","IMPRINT",EDGE,{"derivedFrom":sQuery(id+"F5.wireOp",EDGE,"E18.7.2.0")}),1.0]])]});
            var Q24;
            Q24=makeQuery(id+"F5.imprint","IMPRINT",FACE,{"disambiguationData":[TD([[makeQuery(id+"F5.imprint","IMPRINT",EDGE,{"derivedFrom":sQuery(id+"F5.wireOp",EDGE,"E18.7.3.0")}),1.0]])]});
            var Q25;
            Q25=makeQuery(id+"F5.imprint","IMPRINT",FACE,{"disambiguationData":[TD([[makeQuery(id+"F5.imprint","IMPRINT",EDGE,{"derivedFrom":sQuery(id+"F5.wireOp",EDGE,"E18.6.3.0")}),1.0]])]});
            var Q26;
            Q26=makeQuery(id+"F5.imprint","IMPRINT",FACE,{"disambiguationData":[TD([[makeQuery(id+"F5.imprint","IMPRINT",EDGE,{"derivedFrom":sQuery(id+"F5.wireOp",EDGE,"E18.5.3.0")}),1.0]])]});
            var Q27;
            Q27=makeQuery(id+"F5.imprint","IMPRINT",FACE,{"disambiguationData":[TD([[makeQuery(id+"F5.imprint","IMPRINT",EDGE,{"derivedFrom":sQuery(id+"F5.wireOp",EDGE,"E18.4.3.0")}),1.0]])]});
            var Q28;
            Q28=makeQuery(id+"F5.imprint","IMPRINT",FACE,{"disambiguationData":[TD([[makeQuery(id+"F5.imprint","IMPRINT",EDGE,{"derivedFrom":sQuery(id+"F5.wireOp",EDGE,"E18.3.3.0")}),1.0]])]});
            var Q29;
            Q29=makeQuery(id+"F5.imprint","IMPRINT",FACE,{"disambiguationData":[TD([[makeQuery(id+"F5.imprint","IMPRINT",EDGE,{"derivedFrom":sQuery(id+"F5.wireOp",EDGE,"E18.2.3.0")}),1.0]])]});
            var Q30;
            Q30=makeQuery(id+"F5.imprint","IMPRINT",FACE,{"disambiguationData":[TD([[makeQuery(id+"F5.imprint","IMPRINT",EDGE,{"derivedFrom":sQuery(id+"F5.wireOp",EDGE,"E18.1.3.0")}),1.0]])]});
            var Q31;
            Q31=makeQuery(id+"F5.imprint","IMPRINT",FACE,{"disambiguationData":[TD([[makeQuery(id+"F5.imprint","IMPRINT",EDGE,{"derivedFrom":sQuery(id+"F5.wireOp",EDGE,"E18.0.3.0")}),1.0]])]});
            extrude(context, id + "F7", {"entities" : qUnion([Q0, Q1, Q2, Q3, Q4, Q5, Q6, Q7, Q8, Q9, Q10, Q11, Q12, Q13, Q14, Q15, Q16, Q17, Q18, Q19, Q20, Q21, Q22, Q23, Q24, Q25, Q26, Q27, Q28, Q29, Q30, Q31]), "operationType" : NewBodyOperationType.ADD, "depth" : 2 * mm});
        }
        {
            var Q0;
            Q0=makeQuery(id+"F3.boolean.opBoolean","MERGE",FACE,{"derivedFrom":[makeQuery(id+"F1.opExtrude","SWEPT_FACE",FACE,{"disambiguationData":[OSD([sQuery(id+"F0.wireOp",EDGE,"E0.left")])]}),makeQuery(id+"F3.opExtrude","SWEPT_FACE",FACE,{"disambiguationData":[OSD([sQuery(id+"F2.wireOp",EDGE,"E1.right")])]})]});
            var sketch = newSketch(context, id + "F8", { "sketchPlane" : qUnion([Q0])});
            skLineSegment(sketch, "E19.bottom", {"start": v(-4.5, -17.5) * mm, "end": v(0, -17.5) * mm});
            skLineSegment(sketch, "E19.top", {"start": v(-4.5, 17.5) * mm, "end": v(0, 17.5) * mm});
            skLineSegment(sketch, "E19.left", {"start": v(-4.5, -17.5) * mm, "end": v(-4.5, 17.5) * mm});
            skPoint(sketch, "E19.middle", {"position": v(0, 0) * mm});
            skLineSegment(sketch, "E20", {"start": v(0, 17.5) * mm, "end": v(0, -17.5) * mm});
            skPoint(sketch, "E21.orphan", {"position": v(4.5, 17.5) * mm});
            skPoint(sketch, "E22.orphan", {"position": v(4.5, -17.5) * mm});
            skSolve(sketch);
        }
        {
            var Q0;
            Q0=makeQuery(id+"F8.imprint","IMPRINT",FACE,{"disambiguationData":[TD([[makeQuery(id+"F8.imprint","IMPRINT",EDGE,{"derivedFrom":sQuery(id+"F8.wireOp",EDGE,"E19.bottom")}),1.0]])]});
            extrude(context, id + "F9", {"entities" : qUnion([Q0]), "operationType" : NewBodyOperationType.REMOVE, "endBound" : BoundingType.THROUGH_ALL, "oppositeDirection" : true, "depth" : 25 * mm});
        }
    });
